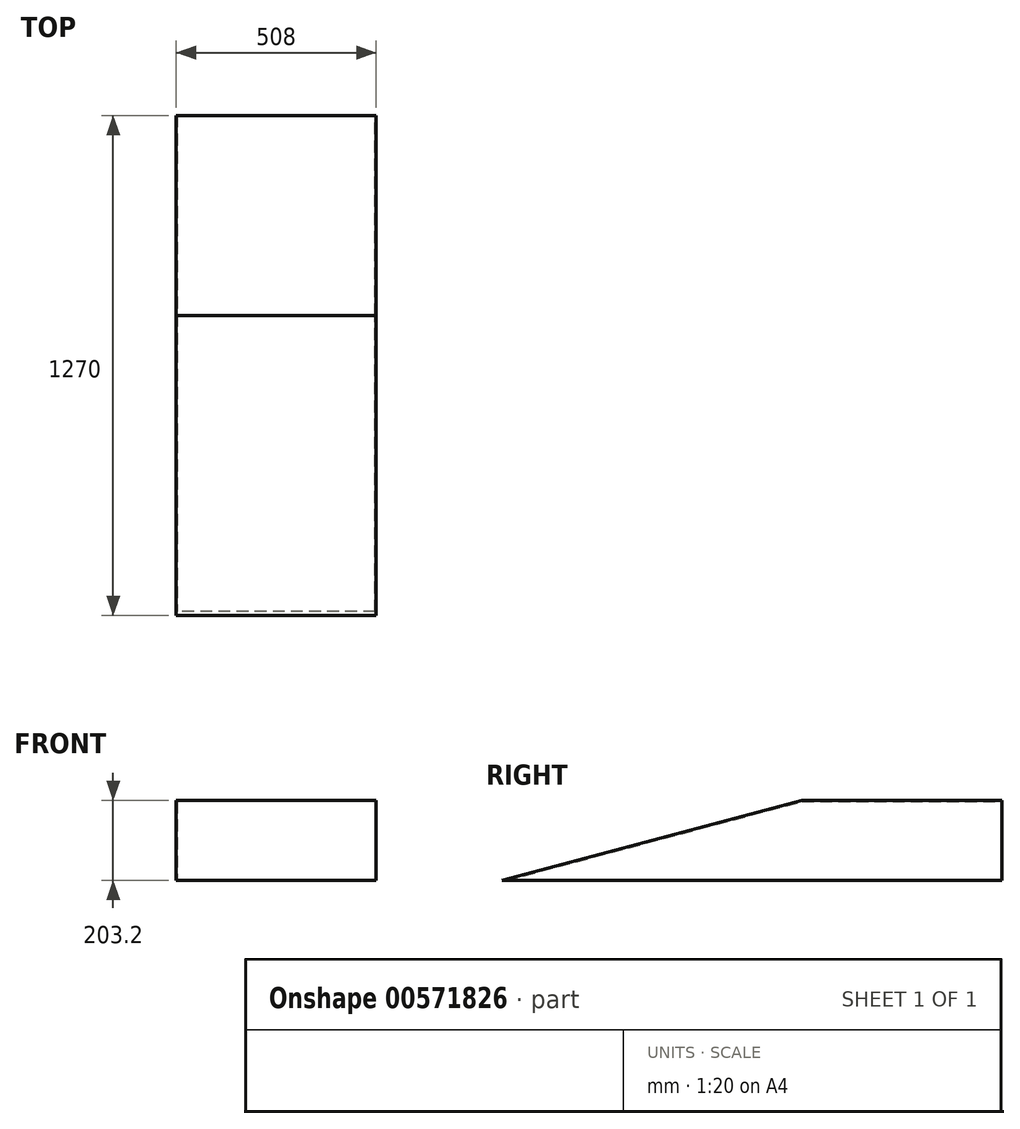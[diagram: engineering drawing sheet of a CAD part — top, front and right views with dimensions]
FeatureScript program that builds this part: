
annotation { "Feature Type Name" : "Feature", "Feature Type Description" : "" }
export const myFeature = defineFeature(function(context is Context, id is Id, definition is map)
    precondition{}
    {
        {
            var Q0;
            Q0=qCreatedBy(makeId("Right.planeOp"),FACE);
            var sketch = newSketch(context, id + "F0", { "sketchPlane" : qUnion([Q0])});
            skLineSegment(sketch, "E0.bottom", {"start": v(0, 0) * mm, "end": v(508, 0) * mm});
            skLineSegment(sketch, "E0.top", {"start": v(0, -203.2) * mm, "end": v(508, -203.2) * mm});
            skLineSegment(sketch, "E0.left", {"start": v(0, 0) * mm, "end": v(0, -203.2) * mm});
            skLineSegment(sketch, "E0.right", {"start": v(508, 0) * mm, "end": v(508, -203.2) * mm});
            skLineSegment(sketch, "E1", {"start": v(0, -203.2) * mm, "end": v(-762, -203.2) * mm});
            skLineSegment(sketch, "E2", {"start": v(-762, -203.2) * mm, "end": v(0, 0) * mm});
            skSolve(sketch);
        }
        {
            var Q0;
            Q0=makeQuery(id+"F0.imprint","IMPRINT",FACE,{"disambiguationData":[TD([[makeQuery(id+"F0.imprint","IMPRINT",EDGE,{"derivedFrom":sQuery(id+"F0.wireOp",EDGE,"E0.left")}),-1.0]])]});
            var Q1;
            Q1=makeQuery(id+"F0.imprint","IMPRINT",FACE,{"disambiguationData":[TD([[makeQuery(id+"F0.imprint","IMPRINT",EDGE,{"derivedFrom":sQuery(id+"F0.wireOp",EDGE,"E0.bottom")}),-1.0]])]});
            extrude(context, id + "F1", {"entities" : qUnion([Q0, Q1]), "depth" : 508 * mm, "offsetDistance" : 25.4 * mm});
        }
        {
            var Q0;
            Q0=makeQuery(id+"F1.opExtrude","SWEPT_FACE",FACE,{"disambiguationData":[OSD([sQuery(id+"F0.wireOp",EDGE,"E0.right")])]});
            var Q1;
            Q1=makeQuery(id+"F1.opExtrude","SWEPT_FACE",FACE,{"disambiguationData":[OSD([sQuery(id+"F0.wireOp",EDGE,"E0.top"),sQuery(id+"F0.wireOp",EDGE,"E1")])]});
            shell(context, id + "F2", {"entities" : qUnion([Q0, Q1]), "thickness" : 2.54 * mm});
        }
    });
